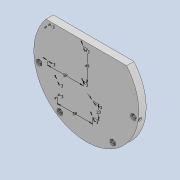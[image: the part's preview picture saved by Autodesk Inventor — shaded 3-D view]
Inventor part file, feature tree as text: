
AUTODESK INVENTOR PART (.ipt)
format: ipt  version: 2020.4 (Build 244396000, 396)  size: 249,856 bytes
history: native  units: mm
features: sketch x11, extrude x10, projected_geometry x5, plane x4
ambient origin geometry x8: Origin, YZ Plane, XZ Plane, XY Plane, X Axis, Y Axis, Z Axis, Center Point
bodies: Solid1 (feature_tree)
feature tree (30):
  extrude  "Extrusion1"  Depth=78.0mm
  extrude  "Extrusion2"  Depth=12.0mm
  extrude  "Extrusion3"  Depth=4.22mm
  extrude  "Extrusion4"  Depth=20.0mm
  extrude  "Extrusion5"  Depth=55.0mm
  extrude  "Extrusion6"  Depth=4.0mm TaperAngle=0.0deg
  plane  "Work Plane1"
  extrude  "Extrusion7"  Depth=5.0mm
  plane  "Work Plane2"
  extrude  "Extrusion8"  Depth=5.0mm TaperAngle=0.0deg
  plane  "Work Plane3"
  extrude  "Extrusion9"  Depth=5.0mm
  plane  "Work Plane4"
  extrude  "Extrusion10"  Depth=5.0mm TaperAngle=0.0deg
  sketch  "Sketch11"  dims[d35=3.0mm d36=2.436418mm d37=5.0mm d38=5.0mm d39=0.0mm d40=3.0mm d41=2.436418mm d42=5.0mm d43=5.0mm d44=0.0mm d45=-2.0mm d46=5.5mm d47=10.0mm d48=0.0mm d49=-2.0mm d50=5.5mm d51=10.0mm d52=0.0mm d53=-2.0mm d54=5.5mm d55=10.0mm d56=0.0mm d57=-2.0mm d58=5.5mm d59=10.0mm d60=0.0mm d69=58.0mm d70=49.0mm d71=3.0mm d72=3.0mm d73=3.0mm d74=3.0mm d75=58.0mm d76=23.0mm d77=3.0mm d78=3.0mm d79=3.0mm d80=3.0mm d81=3.0mm d82=3.0mm d83=3.0mm d84=3.0mm]
  sketch  "Sketch1"  dims[d0=171.6mm d1=78.0mm]
  sketch  "Sketch2"  dims[d2=78.0mm d5=12.0mm]
  projected_geometry  "Projected Loop1"
  sketch  "Sketch3"  dims[d6=4.22mm d7=4.22mm]
  projected_geometry  "Projected Loop2"
  sketch  "Sketch4"  dims[d10=12.0mm d11=20.0mm d13=8.290314mm]
  projected_geometry  "Projected Loop3"
  sketch  "Sketch5"  dims[d15=20.0mm d17=8.290314mm d19=55.0mm]
  projected_geometry  "Projected Loop4"
  sketch  "Sketch6"  dims[d20=12.0mm d21=0.0mm d22=4.0mm d23=0.0mm]
  projected_geometry  "Projected Loop5"
  sketch  "Sketch7"  dims[d24=3.0mm d26=5.0mm]
  sketch  "Sketch8"  dims[d27=2.436418mm d28=5.0mm d29=0.0mm]
  sketch  "Sketch9"  dims[d30=3.0mm d31=5.0mm]
  sketch  "Sketch10"  dims[d32=2.436418mm d33=5.0mm d34=0.0mm]
